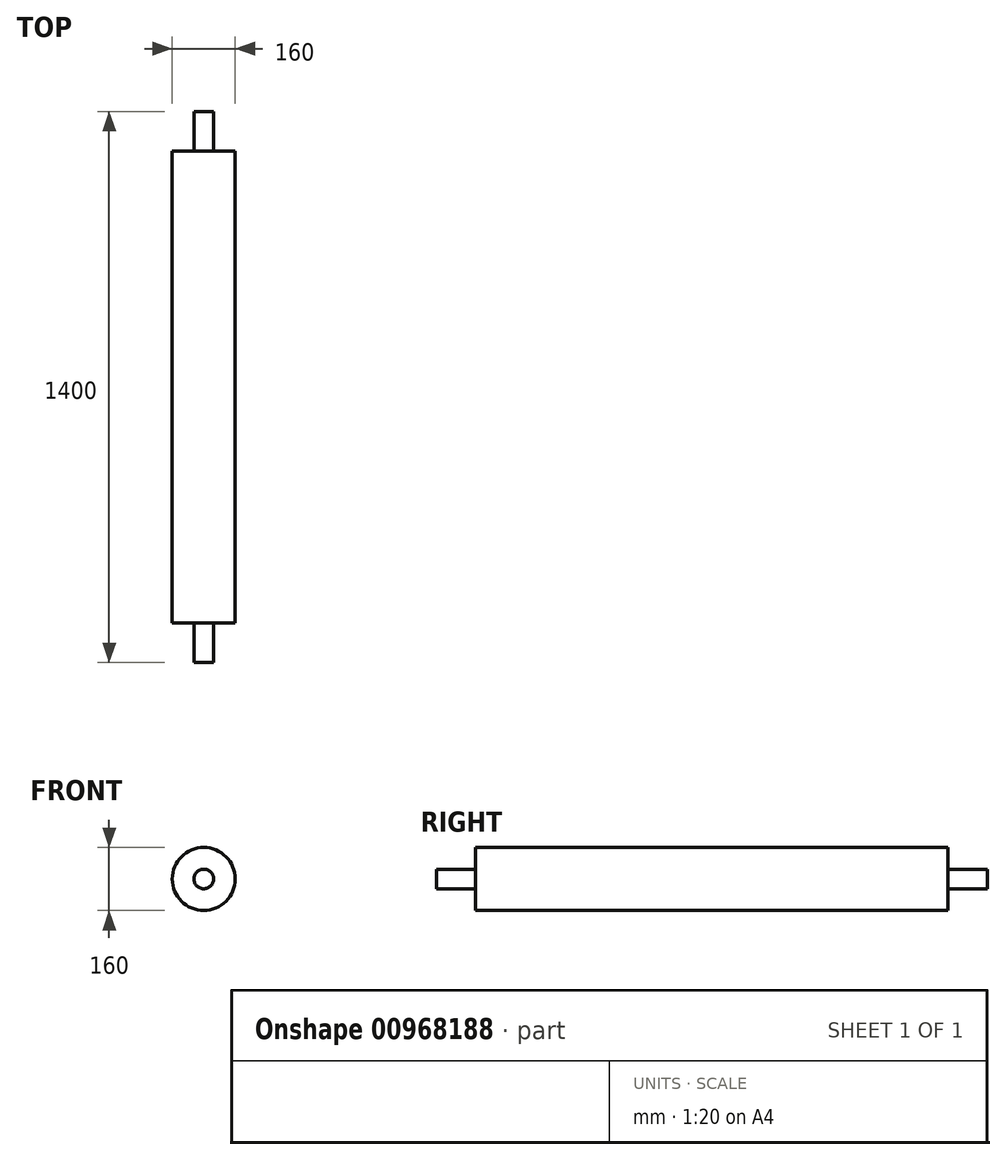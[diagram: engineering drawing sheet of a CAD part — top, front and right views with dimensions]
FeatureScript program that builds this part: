
annotation { "Feature Type Name" : "Feature", "Feature Type Description" : "" }
export const myFeature = defineFeature(function(context is Context, id is Id, definition is map)
    precondition{}
    {
        {
            var Q0;
            Q0=qCreatedBy(makeId("Front.planeOp"),FACE);
            var sketch = newSketch(context, id + "F0", { "sketchPlane" : qUnion([Q0])});
            skCircle(sketch, "E0", {"center": v(0, 0) * mm, "radius": 80 * mm});
            skSolve(sketch);
        }
        {
            var Q0;
            Q0 = qSketchRegion(id + "F0", true);
            extrude(context, id + "F1", {"entities" : qUnion([Q0]), "endBound" : BoundingType.SYMMETRIC, "depth" : 1200 * mm, "offsetDistance" : 25 * mm});
        }
        {
            var Q0;
            Q0=makeQuery(id+"F1.opExtrude","CAP_FACE",FACE,{"disambiguationData":[OSD([sQuery(id+"F0.wireOp",EDGE,"E0")])],"isStart":false});
            var sketch = newSketch(context, id + "F2", { "sketchPlane" : qUnion([Q0])});
            skCircle(sketch, "E1", {"center": v(0, 0) * mm, "radius": 25 * mm});
            skSolve(sketch);
        }
        {
            var Q0;
            Q0 = qSketchRegion(id + "F2", true);
            extrude(context, id + "F3", {"entities" : qUnion([Q0]), "operationType" : NewBodyOperationType.ADD, "depth" : 100 * mm, "offsetDistance" : 25 * mm});
        }
        {
            var Q0;
            Q0=makeQuery(id+"F1.opExtrude","SWEPT_BODY",BODY,{"disambiguationData":[OSD([sQuery(id+"F0.wireOp",EDGE,"E0")])]});
            var Q1;
            Q1=qCreatedBy(makeId("Front.planeOp"),FACE);
            mirror(context, id + "F4", {"operationType" : NewBodyOperationType.ADD, "entities" : qUnion([Q0]), "mirrorPlane" : qUnion([Q1])});
        }
    });
